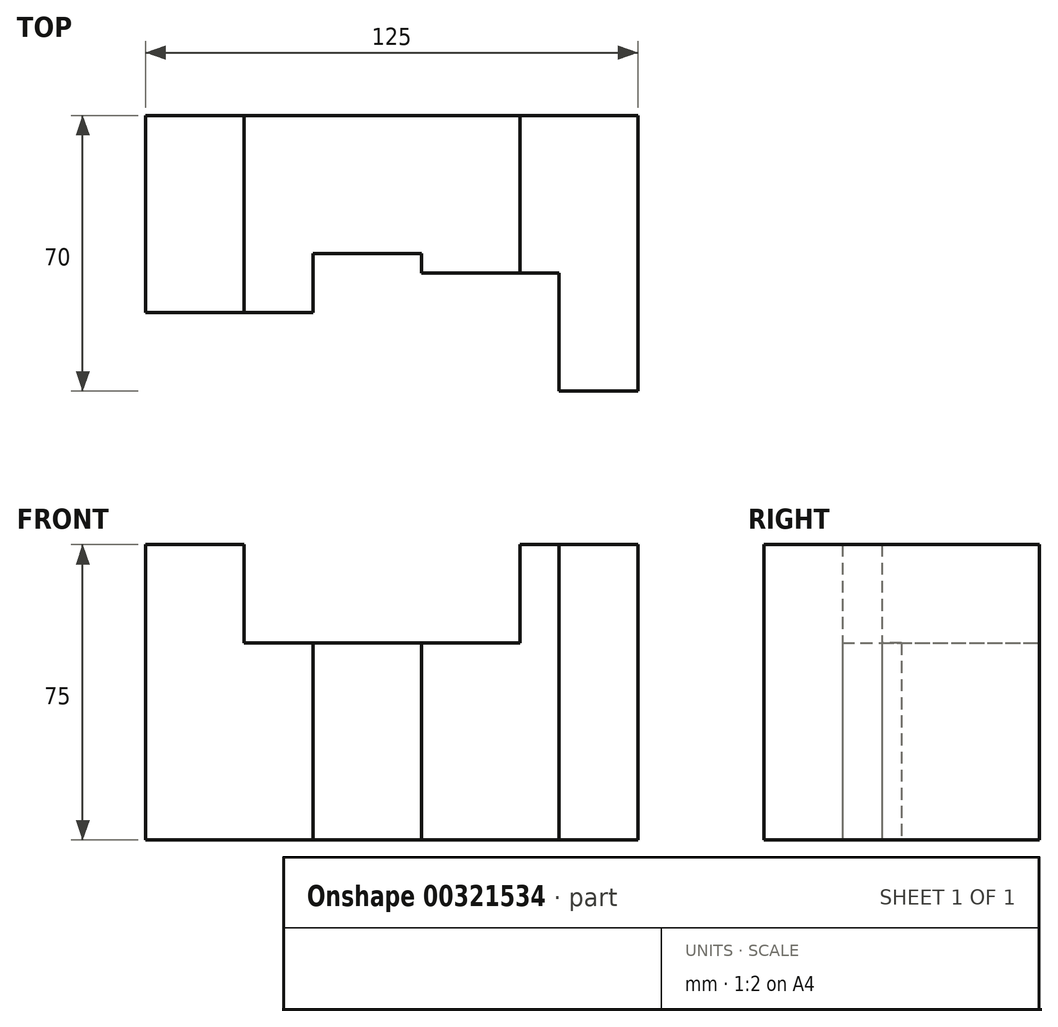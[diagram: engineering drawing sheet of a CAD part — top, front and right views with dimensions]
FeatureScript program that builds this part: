
annotation { "Feature Type Name" : "Feature", "Feature Type Description" : "" }
export const myFeature = defineFeature(function(context is Context, id is Id, definition is map)
    precondition{}
    {
        {
            var Q0;
            Q0=qCreatedBy(makeId("Top.planeOp"),FACE);
            var sketch = newSketch(context, id + "F0", { "sketchPlane" : qUnion([Q0])});
            skLineSegment(sketch, "E0.bottom", {"start": v(0, 0) * mm, "end": v(25, 0) * mm});
            skLineSegment(sketch, "E0.top", {"start": v(0, 50) * mm, "end": v(25, 50) * mm});
            skLineSegment(sketch, "E0.left", {"start": v(0, 0) * mm, "end": v(0, 50) * mm});
            skLineSegment(sketch, "E0.right", {"start": v(25, 0) * mm, "end": v(25, 50) * mm});
            skLineSegment(sketch, "E1", {"start": v(25, 0) * mm, "end": v(42.5, 0) * mm});
            skLineSegment(sketch, "E2", {"start": v(42.5, 0) * mm, "end": v(42.5, 15) * mm});
            skLineSegment(sketch, "E3", {"start": v(42.5, 15) * mm, "end": v(70, 15) * mm});
            skLineSegment(sketch, "E4", {"start": v(70, 15) * mm, "end": v(70, 10) * mm});
            skLineSegment(sketch, "E5", {"start": v(25, 50) * mm, "end": v(125, 50) * mm});
            skLineSegment(sketch, "E6", {"start": v(125, 50) * mm, "end": v(125, -20) * mm});
            skLineSegment(sketch, "E7", {"start": v(125, -20) * mm, "end": v(105, -20) * mm});
            skLineSegment(sketch, "E8", {"start": v(105, -20) * mm, "end": v(105, 10) * mm});
            skLineSegment(sketch, "E9", {"start": v(105, 10) * mm, "end": v(70, 10) * mm});
            skLineSegment(sketch, "E10", {"start": v(95, 10) * mm, "end": v(95, 50) * mm});
            skSolve(sketch);
        }
        {
            var Q0;
            {var subQ0=sQuery(id+"F0.wireOp",EDGE,"E0.right");Q0=makeQuery(id+"F0.imprint","IMPRINT",FACE,{"disambiguationData":[TD([[makeQuery(id+"F0.imprint","IMPRINT",EDGE,{"derivedFrom":subQ0}),-1.0]])]});}
            extrude(context, id + "F1", {"entities" : qUnion([Q0]), "depth" : 50 * mm});
        }
        {
            var Q0;
            Q0=makeQuery(id+"F0.imprint","IMPRINT",FACE,{"disambiguationData":[TD([[makeQuery(id+"F0.imprint","IMPRINT",EDGE,{"derivedFrom":sQuery(id+"F0.wireOp",EDGE,"E0.bottom")}),1.0]])]});
            var Q1;
            {var subQ1=sQuery(id+"F0.wireOp",EDGE,"E6");Q1=makeQuery(id+"F0.imprint","IMPRINT",FACE,{"disambiguationData":[TD([[makeQuery(id+"F0.imprint","IMPRINT",EDGE,{"derivedFrom":subQ1}),-1.0]])]});}
            extrude(context, id + "F2", {"entities" : qUnion([Q0, Q1]), "operationType" : NewBodyOperationType.ADD, "depth" : 75 * mm});
        }
    });
